# Revit family: Sanitary_Accessories_Sanindusa_New-WC-Care-100-Hand-Bar
name_source: partatom
category: Plumbing Fixtures
revit_build: Autodesk Revit 2018 (Build: 20170223_1515(x64)
units: mm (PartAtom-declared; Revit-internal decimal feet)

## family parameters
Always vertical = Yes
Cut with Voids When Loaded = No
OmniClass Number = 23.45.00.00
OmniClass Title = Sanitary, Laundry, and Cleaning Equipment
Part Type = Normal
Room Calculation Point = No
Round Connector Dimension = Use Diameter
Shared = No
Work Plane-Based = No

## types (1)
- Sanitary_Accessories_Sanindusa_New-WC-Care-100-Hand-Bar
    AssetType = Fixed
    BarCode = 5604815900378
    Color = Silver
    Constituents = Fixings not included
150 mm PVC flexible hose; ABS shower bracket, with adjustable height; Fixing Kit.
    Cost = 0 $
    Description = New Wccare hand bar
    Edition number = 1
    Element Type = GRAB BAR: Basic drop-down grab bar, for people with reduced mobility
    Features = Straight grab bar for people with reduced mobility. 
Tube Ø 35mm. For use as a handrail and grab bar for WCs, showers or baths. 
Stainless steel tube for easy maintenance and hygiene. 
40mm gap between the bar and the wall: minimal space prevents the forearm passing between the bar and the wall, reducing the risk of fracture in case of loss of balance.
    Finish = Brushed
    Installation Instructions = https://www.tec.sanindusa.pt
    InstallationDate = 1900-12-31T23:59:59
    Manufacturer = Sanindusa
    ManufacturerName = Sanindusa
    ManufacturerURL = www.tec.sanindusa.pt
    Material = Stainless steel
    ModelNumber = 4297213
    ModelReference = New Wccare
    Name = 100 hand bar new wccare
    NominalHeight = 0 mm  [stored 0 ft]
    NominalLength = 1000 mm  [stored 3.28084 ft]
    NominalWidth = 116 mm  [stored 0.380577 ft]
    Pre-defined type (IFC) = FURNISHING ELEMENT
    Product Guid = d4f09907-d92e-411f-a8f7-be336a114767
    Product data url = https://bimobject.com
    ProductInformation = https://www.tec.sanindusa.pt
    ProductionYear = 2017
    Size = 100x12
    Type (IFC) = IfcFurnitureType
    URL = www.tec.sanindusa.pt
    Uniclass2015Version = Products v1.6
    Version = 2
    WarrantyDescription = https://www.tec.sanindusa.pt
    WarrantyDurationParts = 5
    WarrantyDurationUnit = year
    WarrantyStartDate = 1900-12-31T23:59:59
1900-12-31T23:59:59
    Weight = 1.84 kg

note: [stored X ft] marks values corroborated as IEEE doubles in the binary element streams (Revit-internal decimal feet)

## geometry (parser evidence)
native form markers: Sweep x5
no freeform markers — native parametric forms only
